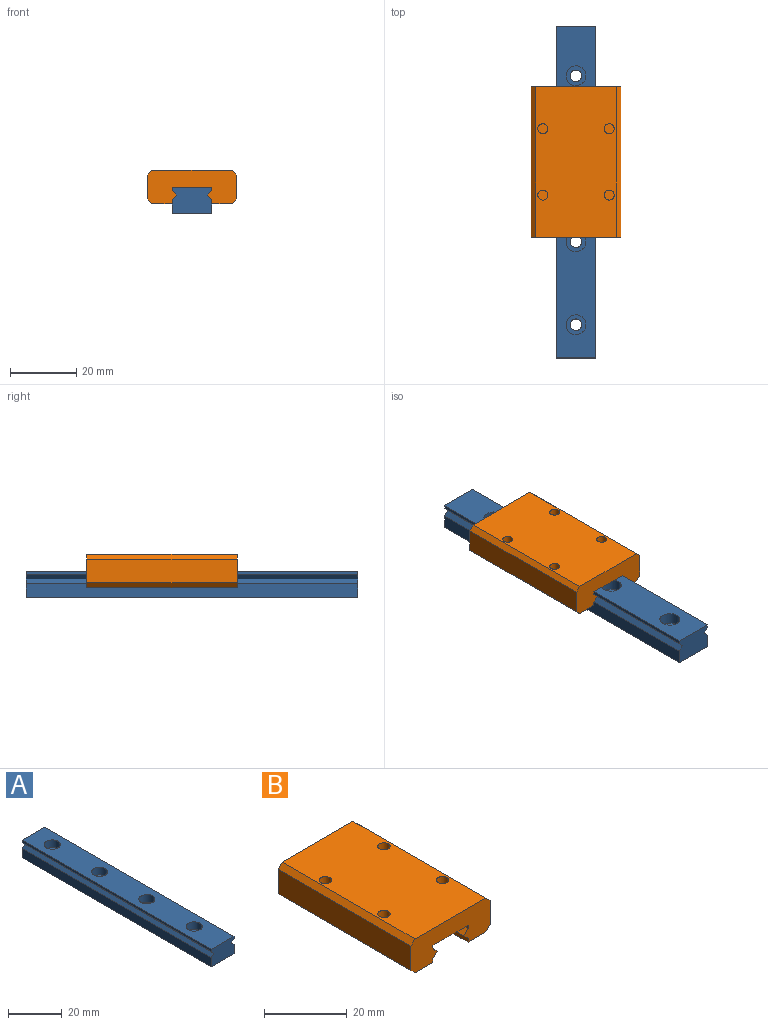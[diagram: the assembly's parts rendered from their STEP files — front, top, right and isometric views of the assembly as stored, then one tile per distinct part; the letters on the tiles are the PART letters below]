
ASSEMBLY  parts=2 mates=1
PART A: 24 faces, bbox 12x100x8 mm
  f0: plane 100x4.17mm, normal (-1,0,0), area 417.2mm2, adj f1,f9,f10,f11
  f1: plane 100x12mm, normal (0,0,-1), area 1161.5mm2, adj f0,f2,f10,f11,f14,f17,f20,f23
  f2: plane 100x4.17mm, normal (1,0,0), area 417.2mm2, adj f1,f3,f10,f11
  f3: plane 100x1.41mm, normal (0.71,0,0.71), area 200mm2, adj f2,f4,f10,f11
  f4: plane 100x1.41mm, normal (0.71,0,-0.71), area 200mm2, adj f3,f5,f10,f11
  f5: plane 100x1mm, normal (1,0,0), area 100mm2, adj f4,f6,f10,f11
  f6: plane 100x12mm, normal (0,0,1), area 1086.9mm2, adj f5,f7,f10,f11,f12,f15,f18,f21
  f7: plane 100x1mm, normal (-1,0,0), area 100mm2, adj f6,f8,f10,f11
  f8: plane 100x1.41mm, normal (-0.71,0,-0.71), area 200mm2, adj f7,f9,f10,f11
  f9: plane 100x1.41mm, normal (-0.71,0,0.71), area 200mm2, adj f0,f8,f10,f11
  f10: plane 12x8mm, normal (0,-1,0), area 92mm2, adj f0,f1,f2,f3,f4,f5,f6,f7
  f11: plane 12x8mm, normal (0,1,0), area 92mm2, adj f0,f1,f2,f3,f4,f5,f6,f7
  f12: cylinder r=3mm len=6mm, axis (0,0,1), area 66mm2, adj f6,f13
  f13: plane 6x6mm, normal (0,0,1), area 18.7mm2, adj f12,f14
  f14: cylinder r=1.75mm len=4.5mm, axis (0,0,1), area 49.5mm2, adj f1,f13
  f15: cylinder r=3mm len=6mm, axis (0,0,1), area 66mm2, adj f6,f16
  f16: plane 6x6mm, normal (0,0,1), area 18.7mm2, adj f15,f17
  f17: cylinder r=1.75mm len=4.5mm, axis (0,0,1), area 49.5mm2, adj f1,f16
  f18: cylinder r=3mm len=6mm, axis (0,0,1), area 66mm2, adj f6,f19
  f19: plane 6x6mm, normal (0,0,1), area 18.7mm2, adj f18,f20
  f20: cylinder r=1.75mm len=4.5mm, axis (0,0,1), area 49.5mm2, adj f1,f19
  f21: cylinder r=3mm len=6mm, axis (0,0,1), area 66mm2, adj f6,f22
  f22: plane 6x6mm, normal (0,0,1), area 18.7mm2, adj f21,f23
  f23: cylinder r=1.75mm len=4.5mm, axis (0,0,1), area 49.5mm2, adj f1,f22
PART B: 28 faces, bbox 27x45.4x10 mm
  f0: plane 45.4x24.18mm, normal (0,0,1), area 1069.6mm2, adj f11,f12,f18,f19,f20,f22,f24,f26
  f1: plane 45.4x1.41mm, normal (0.71,0,0.71), area 90.8mm2, adj f2,f17,f18,f19
  f2: plane 45.4x1mm, normal (1,0,0), area 45.4mm2, adj f1,f3,f18,f19
  f3: plane 45.4x12mm, normal (0,0,-1), area 544.8mm2, adj f2,f4,f18,f19
  f4: plane 45.4x1mm, normal (-1,0,0), area 45.4mm2, adj f3,f5,f18,f19
  f5: plane 45.4x1.41mm, normal (-0.71,0,0.71), area 90.8mm2, adj f4,f6,f18,f19
  f6: plane 45.4x1.41mm, normal (-0.71,0,-0.71), area 90.8mm2, adj f5,f7,f18,f19
  f7: plane 45.4x1.17mm, normal (-1,0,0), area 53.2mm2, adj f6,f8,f18,f19
  f8: plane 45.4x6.09mm, normal (0,0,-1), area 276.5mm2, adj f7,f9,f18,f19
  f9: plane 45.4x1.41mm, normal (0.71,0,-0.71), area 90.4mm2, adj f8,f10,f18,f19
  f10: plane 45.4x7.18mm, normal (1,0,0), area 326.1mm2, adj f9,f11,f18,f19
  f11: plane 45.4x1.41mm, normal (0.71,0,0.71), area 90.4mm2, adj f0,f10,f18,f19
  f12: plane 45.4x1.41mm, normal (-0.71,0,0.71), area 90.4mm2, adj f0,f13,f18,f19
  f13: plane 45.4x7.18mm, normal (-1,0,0), area 326.1mm2, adj f12,f14,f18,f19
  f14: plane 45.4x1.41mm, normal (-0.71,0,-0.71), area 90.4mm2, adj f13,f15,f18,f19
  f15: plane 45.4x6.09mm, normal (0,0,-1), area 276.5mm2, adj f14,f16,f18,f19
  f16: plane 45.4x1.17mm, normal (1,0,0), area 53.2mm2, adj f15,f17,f18,f19
  f17: plane 45.4x1.41mm, normal (0.71,0,-0.71), area 90.8mm2, adj f1,f16,f18,f19
  f18: plane 27x10mm, normal (0,-1,0), area 210mm2, adj f0,f1,f2,f3,f4,f5,f6,f7
  f19: plane 27x10mm, normal (0,1,0), area 210mm2, adj f0,f1,f2,f3,f4,f5,f6,f7
  f20: cylinder r=1.5mm len=3.5mm, axis (0,0,1), area 33mm2, adj f0,f21
  f21: plane 3x3mm, normal (0,0,1), area 7.1mm2, adj f20
  f22: cylinder r=1.5mm len=3.5mm, axis (0,0,1), area 33mm2, adj f0,f23
  f23: plane 3x3mm, normal (0,0,1), area 7.1mm2, adj f22
  f24: cylinder r=1.5mm len=3.5mm, axis (0,0,1), area 33mm2, adj f0,f25
  f25: plane 3x3mm, normal (0,0,1), area 7.1mm2, adj f24
  f26: cylinder r=1.5mm len=3.5mm, axis (0,0,1), area 33mm2, adj f0,f27
  f27: plane 3x3mm, normal (0,0,1), area 7.1mm2, adj f26
PLACE A rot(axis=(0,0,1),180deg) t=(-87.89,104.93,-72.88)mm
PLACE B rot(axis=(0,0,1),180deg) t=(-87.89,141.28,-72.88)mm
MATE slider A.f11 <-> B.f19  axis (0,-1,0) through (-83.3,104.93,-67.29)mm
